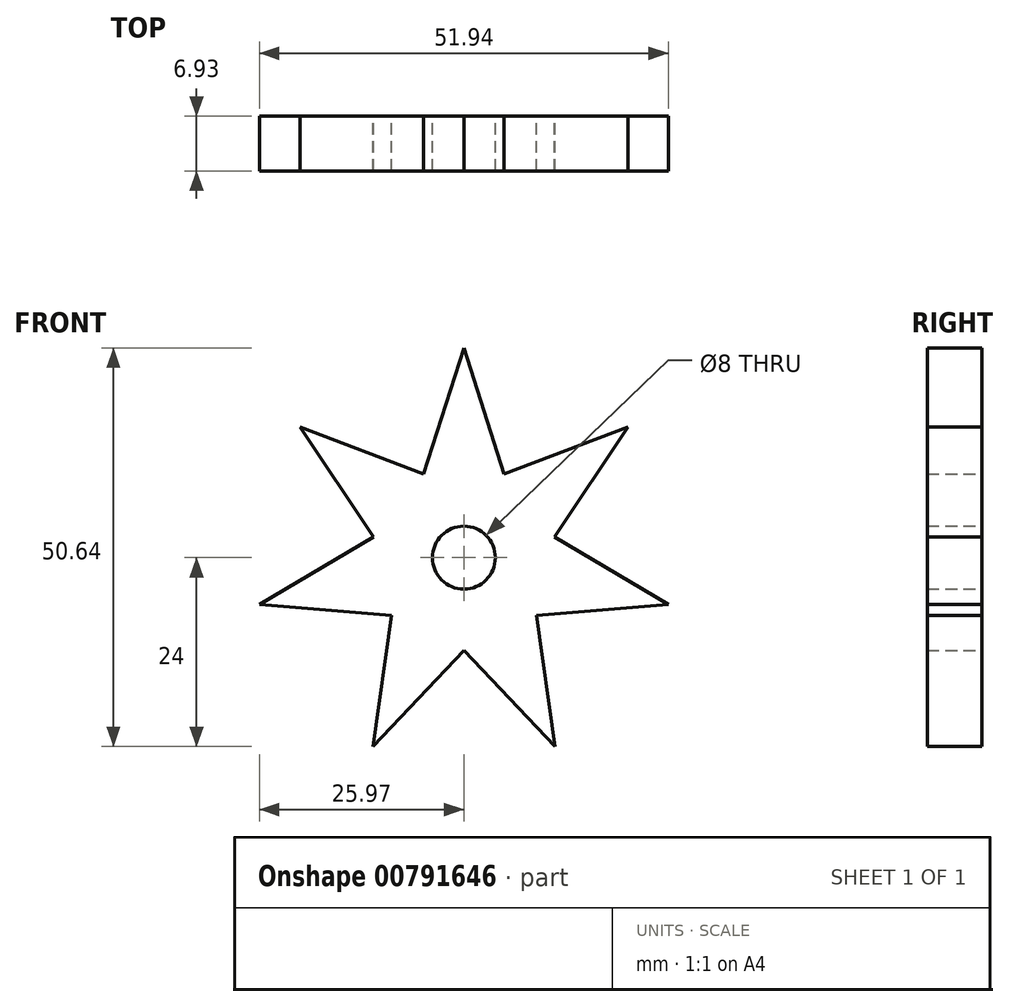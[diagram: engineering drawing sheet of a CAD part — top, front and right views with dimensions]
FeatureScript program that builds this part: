
annotation { "Feature Type Name" : "Feature", "Feature Type Description" : "" }
export const myFeature = defineFeature(function(context is Context, id is Id, definition is map)
    precondition{}
    {
        {
            var Q0;
            Q0=qCreatedBy(makeId("Front.planeOp"),FACE);
            var sketch = newSketch(context, id + "F0", { "sketchPlane" : qUnion([Q0])});
            skCircle(sketch, "E0", {"center": v(0, 0) * mm, "radius": 11.1 * mm});
            skCircle(sketch, "E1", {"center": v(0, 0) * mm, "radius": 4 * mm});
            skLineSegment(sketch, "E2", {"start": v(-5.4, 9.7) * mm, "end": v(0, 26.64) * mm});
            skLineSegment(sketch, "E3", {"start": v(0, 26.64) * mm, "end": v(5.4, 9.7) * mm});
            skLineSegment(sketch, "E4.1.0", {"start": v(-20.83, 16.6) * mm, "end": v(-4.21, 10.27) * mm});
            skLineSegment(sketch, "E4.1.1", {"start": v(-10.95, 1.82) * mm, "end": v(-20.83, 16.6) * mm});
            skLineSegment(sketch, "E4.2.0", {"start": v(-25.97, -5.93) * mm, "end": v(-10.66, 3.1) * mm});
            skLineSegment(sketch, "E4.2.1", {"start": v(-8.25, -7.42) * mm, "end": v(-25.97, -5.93) * mm});
            skLineSegment(sketch, "E4.3.0", {"start": v(-11.56, -24) * mm, "end": v(-9.07, -6.4) * mm});
            skLineSegment(sketch, "E4.3.1", {"start": v(0.66, -11.08) * mm, "end": v(-11.56, -24) * mm});
            skLineSegment(sketch, "E4.4.0", {"start": v(11.56, -24) * mm, "end": v(-0.66, -11.08) * mm});
            skLineSegment(sketch, "E4.4.1", {"start": v(9.07, -6.4) * mm, "end": v(11.56, -24) * mm});
            skLineSegment(sketch, "E5.2.5.0", {"start": v(25.97, -5.93) * mm, "end": v(8.25, -7.42) * mm});
            skLineSegment(sketch, "E5.3.5.0", {"start": v(10.66, 3.1) * mm, "end": v(25.97, -5.93) * mm});
            skLineSegment(sketch, "E5.2.6.0", {"start": v(20.83, 16.6) * mm, "end": v(10.95, 1.82) * mm});
            skLineSegment(sketch, "E5.3.6.0", {"start": v(4.21, 10.27) * mm, "end": v(20.83, 16.6) * mm});
            skSolve(sketch);
        }
        {
            var Q0;
            Q0 = qSketchRegion(id + "F0", true);
            var Q1;
            Q1=makeQuery(id+"F0.imprint","IMPRINT",FACE,{"disambiguationData":[TD([[makeQuery(id+"F0.imprint","IMPRINT",EDGE,{"derivedFrom":sQuery(id+"F0.wireOp",EDGE,"E1")}),-1.0]])]});
            extrude(context, id + "F1", {"entities" : qUnion([Q0, Q1]), "depth" : 6.93 * mm, "offsetDistance" : 25.4 * mm});
        }
    });
